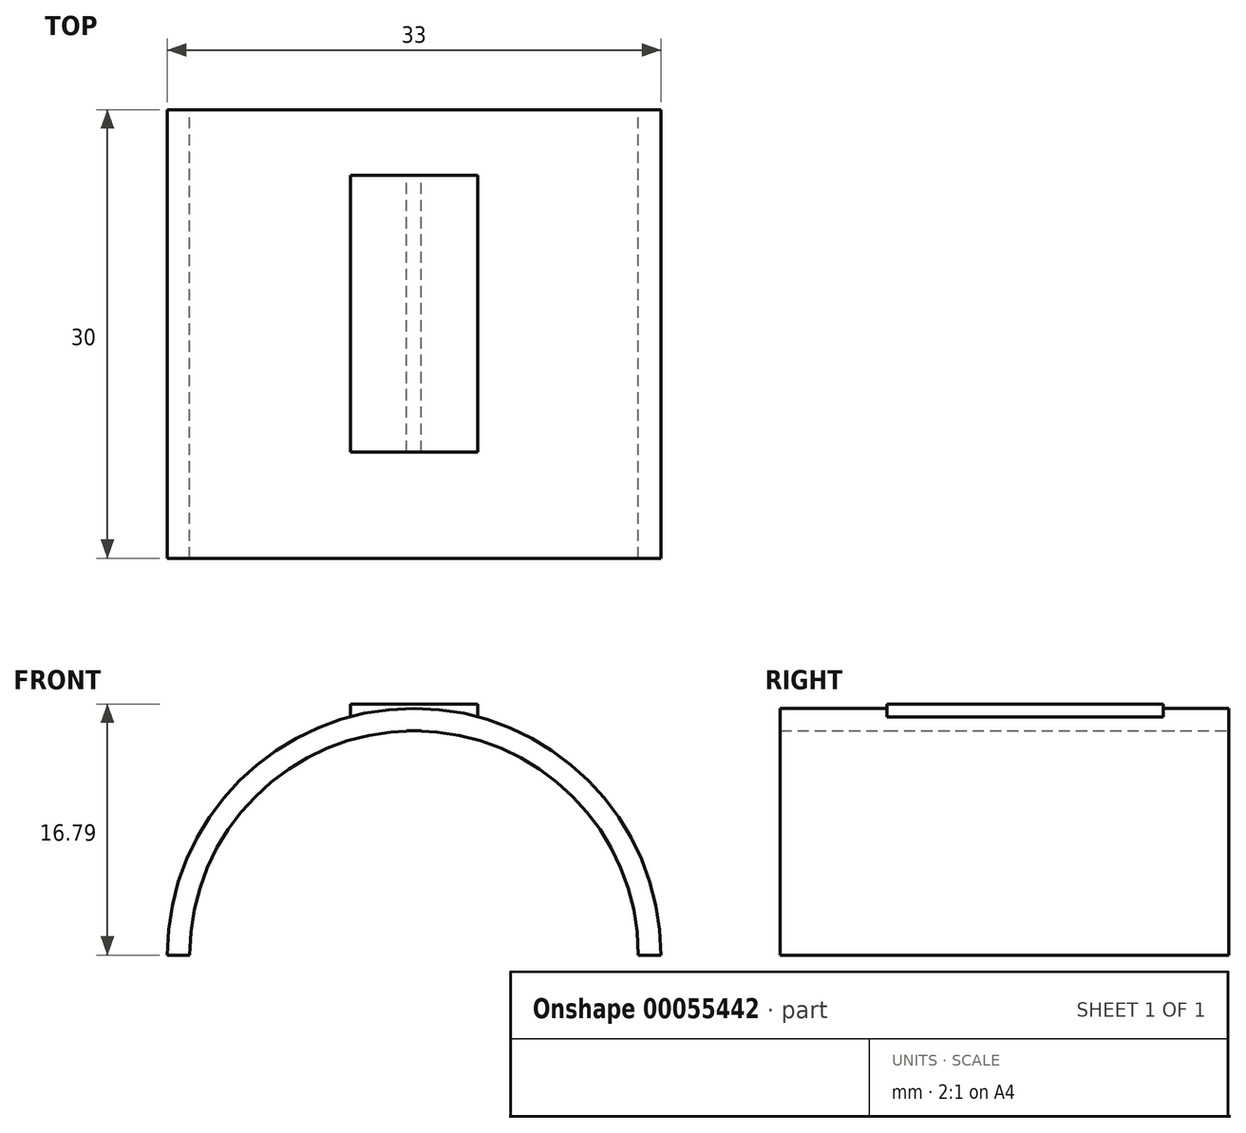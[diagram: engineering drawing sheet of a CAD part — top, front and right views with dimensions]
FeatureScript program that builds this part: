
annotation { "Feature Type Name" : "Feature", "Feature Type Description" : "" }
export const myFeature = defineFeature(function(context is Context, id is Id, definition is map)
    precondition{}
    {
        {
            var Q0;
            Q0=qCreatedBy(makeId("Front.planeOp"),FACE);
            var sketch = newSketch(context, id + "F0", { "sketchPlane" : qUnion([Q0])});
            skArc(sketch, "E0", {"start": v(15, 0) * mm, "mid": v(0, 15) * mm, "end": v(-15, 0) * mm});
            skArc(sketch, "E1", {"start": v(16.5, 0) * mm, "mid": v(0, 16.5) * mm, "end": v(-16.5, 0) * mm});
            skLineSegment(sketch, "E2", {"start": v(-16.5, 0) * mm, "end": v(-15, 0) * mm});
            skLineSegment(sketch, "E3.trimOffspring", {"start": v(15, 0) * mm, "end": v(16.5, 0) * mm});
            skSolve(sketch);
        }
        {
            var Q0;
            Q0 = qSketchRegion(id + "F0", true);
            extrude(context, id + "F1", {"entities" : qUnion([Q0]), "depth" : 30 * mm});
        }
        {
            var Q0;
            Q0=qCreatedBy(makeId("Front.planeOp"),FACE);
            var sketch = newSketch(context, id + "F2", { "sketchPlane" : qUnion([Q0])});
            skLineSegment(sketch, "E4", {"start": v(0, 0) * mm, "end": v(0, 15.8) * mm});
            skSolve(sketch);
        }
        {
            var Q0;
            Q0=sQuery(id+"F2.wireOp",VERTEX,"E4.end");
            var Q1;
            Q1=sQuery(id+"F2.wireOp",EDGE,"E4");
            cPlane(context, id + "F3", {"entities" : qUnion([Q0, Q1]), "cplaneType" : CPlaneType.LINE_POINT, "offset" : 150 * mm, "width" : 150 * mm, "height" : 150 * mm});
        }
        {
            var Q0;
            Q0=qCreatedBy(id+"F3.planeOp",FACE);
            var sketch = newSketch(context, id + "F4", { "sketchPlane" : qUnion([Q0])});
            skLineSegment(sketch, "E5.rect.bottom", {"start": v(4.26, -22.88) * mm, "end": v(-4.26, -22.88) * mm});
            skLineSegment(sketch, "E5.rect.top", {"start": v(4.26, -4.38) * mm, "end": v(-4.26, -4.38) * mm});
            skLineSegment(sketch, "E5.rect.left", {"start": v(4.26, -22.88) * mm, "end": v(4.26, -4.38) * mm});
            skLineSegment(sketch, "E5.rect.right", {"start": v(-4.26, -22.88) * mm, "end": v(-4.26, -4.38) * mm});
            skPoint(sketch, "E5.rect.middle", {"position": v(0, -13.63) * mm});
            skSolve(sketch);
        }
        {
            var Q0;
            Q0 = qSketchRegion(id + "F4", true);
            extrude(context, id + "F5", {"entities" : qUnion([Q0]), "depth" : 1 * mm});
        }
        {
            var Q0;
            Q0=makeQuery(id+"F5.opExtrude","CAP_FACE",FACE,{"disambiguationData":[OSD([sQuery(id+"F4.wireOp",EDGE,"E5.rect.bottom"),sQuery(id+"F4.wireOp",EDGE,"E5.rect.top"),sQuery(id+"F4.wireOp",EDGE,"E5.rect.left"),sQuery(id+"F4.wireOp",EDGE,"E5.rect.right")])],"isStart":false});
            var sketch = newSketch(context, id + "F6", { "sketchPlane" : qUnion([Q0])});
            skLineSegment(sketch, "E6.bottom", {"start": v(-4.26, -4.38) * mm, "end": v(4.26, -4.38) * mm});
            skLineSegment(sketch, "E6.top", {"start": v(-4.26, -22.88) * mm, "end": v(4.26, -22.88) * mm});
            skLineSegment(sketch, "E6.left", {"start": v(-4.26, -4.38) * mm, "end": v(-4.26, -22.88) * mm});
            skLineSegment(sketch, "E6.right", {"start": v(4.26, -4.38) * mm, "end": v(4.26, -22.88) * mm});
            skSolve(sketch);
        }
        {
            var Q0;
            Q0 = qSketchRegion(id + "F6", true);
            extrude(context, id + "F7", {"entities" : qUnion([Q0]), "operationType" : NewBodyOperationType.ADD, "oppositeDirection" : true, "depth" : 1.8 * mm});
        }
    });
